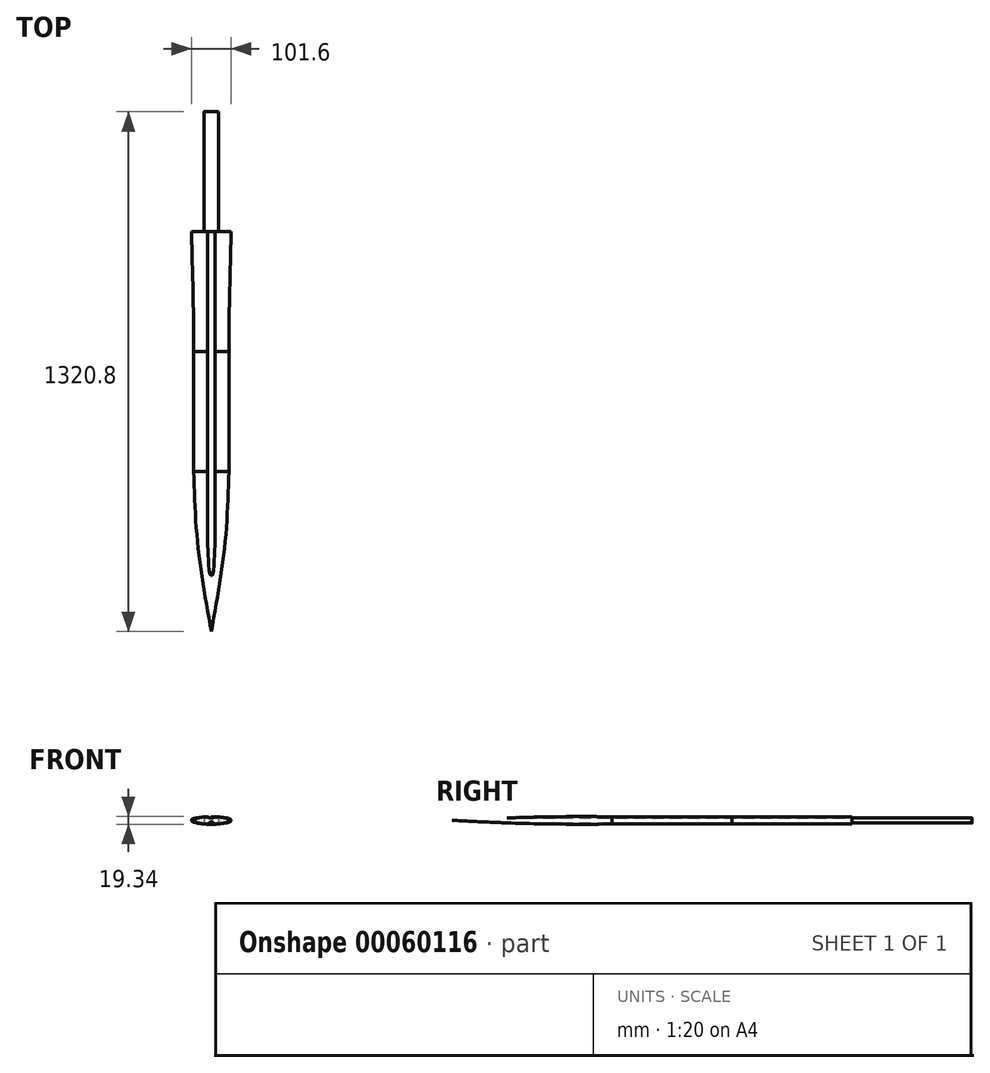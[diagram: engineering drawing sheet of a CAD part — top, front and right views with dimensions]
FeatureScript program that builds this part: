
annotation { "Feature Type Name" : "Feature", "Feature Type Description" : "" }
export const myFeature = defineFeature(function(context is Context, id is Id, definition is map)
    precondition{}
    {
        {
            var Q0;
            Q0=qCreatedBy(makeId("Front.planeOp"),FACE);
            var sketch = newSketch(context, id + "F0", { "sketchPlane" : qUnion([Q0])});
            skLineSegment(sketch, "E0", {"start": v(-50.8, 0) * mm, "end": v(50.8, 0) * mm, "construction": true});
            skLineSegment(sketch, "E1", {"start": v(0, 9.53) * mm, "end": v(0, -9.53) * mm, "construction": true});
            skEllipse(sketch, "E2", {"center": v(0, 0) * mm, "majorRadius": 50.8 * mm, "minorRadius": 9.53 * mm, "majorAxis": v(1, 0)});
            skSolve(sketch);
        }
        {
            var Q0;
            Q0=qCreatedBy(makeId("Front.planeOp"),FACE);
            cPlane(context, id + "F1", {"entities" : qUnion([Q0]), "cplaneType" : CPlaneType.OFFSET, "offset" : 304.8 * mm, "width" : 152.4 * mm, "height" : 152.4 * mm});
        }
        {
            var Q0;
            Q0=qCreatedBy(id+"F1.planeOp",FACE);
            var sketch = newSketch(context, id + "F2", { "sketchPlane" : qUnion([Q0])});
            skLineSegment(sketch, "E3.0", {"start": v(-50.8, 0) * mm, "end": v(50.8, 0) * mm, "construction": true});
            skLineSegment(sketch, "E4.0", {"start": v(0, 9.53) * mm, "end": v(0, -9.53) * mm, "construction": true});
            skEllipse(sketch, "E5", {"center": v(0, 0) * mm, "majorRadius": 44.45 * mm, "minorRadius": 9.53 * mm, "majorAxis": v(1, 0)});
            skLineSegment(sketch, "E6", {"start": v(-44.45, 0) * mm, "end": v(44.45, 0) * mm, "construction": true});
            skSolve(sketch);
        }
        {
            var Q0;
            Q0=qCreatedBy(id+"F1.planeOp",FACE);
            cPlane(context, id + "F3", {"entities" : qUnion([Q0]), "cplaneType" : CPlaneType.OFFSET, "offset" : 304.8 * mm, "width" : 152.4 * mm, "height" : 152.4 * mm});
        }
        {
            var Q0;
            Q0=qCreatedBy(id+"F3.planeOp",FACE);
            var sketch = newSketch(context, id + "F4", { "sketchPlane" : qUnion([Q0])});
            skPoint(sketch, "E7.0", {"position": v(0, 0) * mm});
            skLineSegment(sketch, "E8.0", {"start": v(-50.8, 0) * mm, "end": v(50.8, 0) * mm, "construction": true});
            skLineSegment(sketch, "E9.0", {"start": v(0, 9.53) * mm, "end": v(0, -9.53) * mm, "construction": true});
            skEllipse(sketch, "E10.0", {"center": v(0, 0) * mm, "majorRadius": 44.45 * mm, "minorRadius": 9.53 * mm, "majorAxis": v(1, 0)});
            skSolve(sketch);
        }
        {
            var Q0;
            Q0=qCreatedBy(id+"F3.planeOp",FACE);
            cPlane(context, id + "F5", {"entities" : qUnion([Q0]), "cplaneType" : CPlaneType.OFFSET, "offset" : 406.4 * mm, "width" : 152.4 * mm, "height" : 152.4 * mm});
        }
        {
            var Q0;
            Q0=qCreatedBy(id+"F5.planeOp",FACE);
            var sketch = newSketch(context, id + "F6", { "sketchPlane" : qUnion([Q0])});
            skPoint(sketch, "E11.0", {"position": v(0, 0) * mm});
            skSolve(sketch);
        }
        {
            var Q0;
            Q0=makeQuery(id+"F2.imprint","IMPRINT",FACE,{"disambiguationData":[TD([[makeQuery(id+"F2.imprint","IMPRINT",EDGE,{"derivedFrom":sQuery(id+"F2.wireOp",EDGE,"E5")}),1.0]])]});
            var Q1;
            Q1=makeQuery(id+"F0.imprint","IMPRINT",FACE,{"disambiguationData":[TD([[makeQuery(id+"F0.imprint","IMPRINT",EDGE,{"derivedFrom":sQuery(id+"F0.wireOp",EDGE,"E2")}),1.0]])]});
            loft(context, id + "F7", {"sheetProfilesArray" : [{ "sheetProfileEntities" : qUnion([Q0]) }, { "sheetProfileEntities" : qUnion([Q1]) }]});
        }
        {
            var Q0;
            Q0=makeQuery(id+"F2.imprint","IMPRINT",FACE,{"disambiguationData":[TD([[makeQuery(id+"F2.imprint","IMPRINT",EDGE,{"derivedFrom":sQuery(id+"F2.wireOp",EDGE,"E5")}),1.0]])]});
            var Q1;
            Q1=makeQuery(id+"F4.imprint","IMPRINT",FACE,{"disambiguationData":[TD([[makeQuery(id+"F4.imprint","IMPRINT",EDGE,{"derivedFrom":sQuery(id+"F4.wireOp",EDGE,"E10.0")}),1.0]])]});
            var Q2;
            Q2=sQuery(id+"F2.wireOp",EDGE,"E5");
            var Q3;
            Q3=sQuery(id+"F4.wireOp",EDGE,"E10.0");
            loft(context, id + "F8", {"operationType" : NewBodyOperationType.ADD, "sheetProfilesArray" : [{ "sheetProfileEntities" : qUnion([Q0]) }, { "sheetProfileEntities" : qUnion([Q1]) }], "wireProfilesArray" : [{ "wireProfileEntities" : qUnion([Q2]) }, { "wireProfileEntities" : qUnion([Q3]) }]});
        }
        {
            var Q0;
            Q0=qCreatedBy(makeId("Top.planeOp"),FACE);
            var sketch = newSketch(context, id + "F9", { "sketchPlane" : qUnion([Q0])});
            skLineSegment(sketch, "E12.0", {"start": v(-44.45, -609.6) * mm, "end": v(44.45, -609.6) * mm});
            skLineSegment(sketch, "E13.0", {"start": v(-44.45, -304.8) * mm, "end": v(44.45, -304.8) * mm});
            skLineSegment(sketch, "E14", {"start": v(44.45, -304.8) * mm, "end": v(44.45, -609.6) * mm, "construction": true});
            skLineSegment(sketch, "E15", {"start": v(-44.45, -304.8) * mm, "end": v(-44.45, -609.6) * mm, "construction": true});
            skPoint(sketch, "E16.0", {"position": v(0, -1016) * mm});
            skArc(sketch, "E17", {"start": v(44.45, -609.6) * mm, "mid": v(33.3, -814.01) * mm, "end": v(0, -1016) * mm, "construction": true});
            skArc(sketch, "E18", {"start": v(-44.45, -609.6) * mm, "mid": v(-33.3, -814.01) * mm, "end": v(0, -1016) * mm, "construction": true});
            skSolve(sketch);
        }
        {
            var Q0;
            Q0=qCreatedBy(makeId("Right.planeOp"),FACE);
            var sketch = newSketch(context, id + "F10", { "sketchPlane" : qUnion([Q0])});
            skLineSegment(sketch, "E19.0", {"start": v(-609.6, -9.53) * mm, "end": v(-609.6, 9.53) * mm});
            skLineSegment(sketch, "E20.0", {"start": v(-304.8, -9.53) * mm, "end": v(-304.8, 9.53) * mm});
            skLineSegment(sketch, "E21", {"start": v(-304.8, 9.53) * mm, "end": v(-609.6, 9.53) * mm, "construction": true});
            skLineSegment(sketch, "E22", {"start": v(-304.8, -9.53) * mm, "end": v(-609.6, -9.53) * mm, "construction": true});
            skPoint(sketch, "E23.0", {"position": v(-1016, 0) * mm});
            skArc(sketch, "E24", {"start": v(-609.6, 9.53) * mm, "mid": v(-812.86, 7.14) * mm, "end": v(-1016, 0) * mm, "construction": true});
            skArc(sketch, "E25", {"start": v(-609.6, -9.53) * mm, "mid": v(-812.86, -7.14) * mm, "end": v(-1016, 0) * mm, "construction": true});
            skSolve(sketch);
        }
        {
            var Q0;
            Q0=makeQuery(id+"F4.imprint","IMPRINT",FACE,{"disambiguationData":[TD([[makeQuery(id+"F4.imprint","IMPRINT",EDGE,{"derivedFrom":sQuery(id+"F4.wireOp",EDGE,"E10.0")}),1.0]])]});
            cPlane(context, id + "F11", {"entities" : qUnion([Q0]), "cplaneType" : CPlaneType.OFFSET, "offset" : 152.4 * mm, "width" : 152.4 * mm, "height" : 152.4 * mm});
        }
        {
            var Q0;
            Q0=qCreatedBy(id+"F11.planeOp",FACE);
            var sketch = newSketch(context, id + "F12", { "sketchPlane" : qUnion([Q0])});
            skLineSegment(sketch, "E26.0", {"start": v(44.45, 0) * mm, "end": v(0, 0) * mm, "construction": true});
            skLineSegment(sketch, "E27.0", {"start": v(-44.45, 0) * mm, "end": v(0, 0) * mm, "construction": true});
            skLineSegment(sketch, "E28.0", {"start": v(0, -9.53) * mm, "end": v(0, 0) * mm, "construction": true});
            skLineSegment(sketch, "E29.0", {"start": v(0, 9.53) * mm, "end": v(0, 0) * mm, "construction": true});
            skEllipse(sketch, "E30", {"center": v(0, 0) * mm, "majorRadius": 37.45 * mm, "minorRadius": 9.53 * mm, "majorAxis": v(1, 0)});
            skSolve(sketch);
        }
        {
            var Q0;
            Q0=makeQuery(id+"F4.imprint","IMPRINT",FACE,{"disambiguationData":[TD([[makeQuery(id+"F4.imprint","IMPRINT",EDGE,{"derivedFrom":sQuery(id+"F4.wireOp",EDGE,"E10.0")}),1.0]])]});
            var Q1;
            Q1=makeQuery(id+"F12.imprint","IMPRINT",FACE,{"disambiguationData":[TD([[makeQuery(id+"F12.imprint","IMPRINT",EDGE,{"derivedFrom":sQuery(id+"F12.wireOp",EDGE,"E30")}),1.0]])]});
            var Q2;
            Q2=sQuery(id+"F9.wireOp",VERTEX,"E16.0");
            loft(context, id + "F13", {"operationType" : NewBodyOperationType.ADD, "sheetProfilesArray" : [{ "sheetProfileEntities" : qUnion([Q0]) }, { "sheetProfileEntities" : qUnion([Q1]) }, { "sheetProfileEntities" : qUnion([Q2]) }]});
        }
        {
            var Q0;
            Q0=qCreatedBy(makeId("Front.planeOp"),FACE);
            var sketch = newSketch(context, id + "F14", { "sketchPlane" : qUnion([Q0])});
            skLineSegment(sketch, "E31", {"start": v(0, 12.7) * mm, "end": v(0, -12.7) * mm, "construction": true});
            skLineSegment(sketch, "E32", {"start": v(69.43, 0) * mm, "end": v(-69.43, 0) * mm, "construction": true});
            skLineSegment(sketch, "E33.rect.bottom", {"start": v(-9.52, 9.53) * mm, "end": v(9.53, 9.53) * mm, "construction": true});
            skLineSegment(sketch, "E33.rect.top", {"start": v(-9.52, -9.53) * mm, "end": v(9.52, -9.53) * mm, "construction": true});
            skLineSegment(sketch, "E33.rect.left", {"start": v(-9.52, 9.53) * mm, "end": v(-9.53, -9.53) * mm, "construction": true});
            skLineSegment(sketch, "E33.rect.right", {"start": v(9.53, 9.53) * mm, "end": v(9.52, -9.53) * mm, "construction": true});
            skPoint(sketch, "E33.rect.middle", {"position": v(0, 0) * mm});
            skEllipse(sketch, "E34", {"center": v(0, 9.53) * mm, "majorRadius": 9.52 * mm, "minorRadius": 3.17 * mm, "majorAxis": v(-1, 0)});
            skEllipse(sketch, "E35.MirrorC", {"center": v(0, -9.53) * mm, "majorRadius": 9.52 * mm, "minorRadius": 3.17 * mm, "majorAxis": v(-1, 0)});
            skSolve(sketch);
        }
        {
            var Q0;
            Q0=makeQuery(id+"F14.imprint","IMPRINT",FACE,{"disambiguationData":[TD([[makeQuery(id+"F14.imprint","IMPRINT",EDGE,{"derivedFrom":sQuery(id+"F14.wireOp",EDGE,"E34")}),1.0]])]});
            var Q1;
            Q1=makeQuery(id+"F14.imprint","IMPRINT",FACE,{"disambiguationData":[TD([[makeQuery(id+"F14.imprint","IMPRINT",EDGE,{"derivedFrom":sQuery(id+"F14.wireOp",EDGE,"E35.MirrorC")}),1.0]])]});
            extrude(context, id + "F15", {"entities" : qUnion([Q0, Q1]), "operationType" : NewBodyOperationType.REMOVE, "depth" : 914.4 * mm});
        }
        {
            var Q0;
            Q0=makeQuery(id+"F7.opLoft","CAP_FACE",FACE,{"disambiguationData":[OSD([makeQuery(id+"F0.imprint","IMPRINT",FACE,{"disambiguationData":[TD([[makeQuery(id+"F0.imprint","IMPRINT",EDGE,{"derivedFrom":sQuery(id+"F0.wireOp",EDGE,"E2")}),1.0]])]})])],"isStart":true});
            var sketch = newSketch(context, id + "F16", { "sketchPlane" : qUnion([Q0])});
            skLineSegment(sketch, "E36.rect.bottom", {"start": v(19.05, 6.35) * mm, "end": v(-19.05, 6.35) * mm});
            skLineSegment(sketch, "E36.rect.top", {"start": v(19.05, -6.35) * mm, "end": v(-19.05, -6.35) * mm});
            skLineSegment(sketch, "E36.rect.left", {"start": v(19.05, 6.35) * mm, "end": v(19.05, -6.35) * mm});
            skLineSegment(sketch, "E36.rect.right", {"start": v(-19.05, 6.35) * mm, "end": v(-19.05, -6.35) * mm});
            skPoint(sketch, "E36.rect.middle", {"position": v(0, 0) * mm});
            skSolve(sketch);
        }
        {
            var Q0;
            {var subQ3=sQuery(id+"F16.wireOp",EDGE,"E36.rect.left");Q0=makeQuery(id+"F16.imprint","IMPRINT",FACE,{"disambiguationData":[TD([[makeQuery(id+"F16.imprint","IMPRINT",EDGE,{"derivedFrom":subQ3}),-1.0]])]});}
            extrude(context, id + "F17", {"entities" : qUnion([Q0]), "operationType" : NewBodyOperationType.ADD, "depth" : 304.8 * mm});
        }
        {
            var Q0;
            Q0=makeQuery(id+"F17.opExtrude","SWEPT_EDGE",EDGE,{"disambiguationData":[OSD([sQuery(id+"F16.wireOp",EDGE,"E36.rect.bottom"),sQuery(id+"F16.wireOp",EDGE,"E36.rect.left")])]});
            var Q1;
            Q1=makeQuery(id+"F17.opExtrude","SWEPT_EDGE",EDGE,{"disambiguationData":[OSD([sQuery(id+"F16.wireOp",EDGE,"E36.rect.top"),sQuery(id+"F16.wireOp",EDGE,"E36.rect.left")])]});
            var Q2;
            Q2=makeQuery(id+"F17.opExtrude","SWEPT_EDGE",EDGE,{"disambiguationData":[OSD([sQuery(id+"F16.wireOp",EDGE,"E36.rect.bottom"),sQuery(id+"F16.wireOp",EDGE,"E36.rect.right")])]});
            var Q3;
            Q3=makeQuery(id+"F17.opExtrude","SWEPT_EDGE",EDGE,{"disambiguationData":[OSD([sQuery(id+"F16.wireOp",EDGE,"E36.rect.top"),sQuery(id+"F16.wireOp",EDGE,"E36.rect.right")])]});
            fillet(context, id + "F18", {"entities" : qUnion([Q0, Q1, Q2, Q3]), "radius" : 3.8 * mm, "tangentPropagation" : true, "allowEdgeOverflow" : false});
        }
    });
